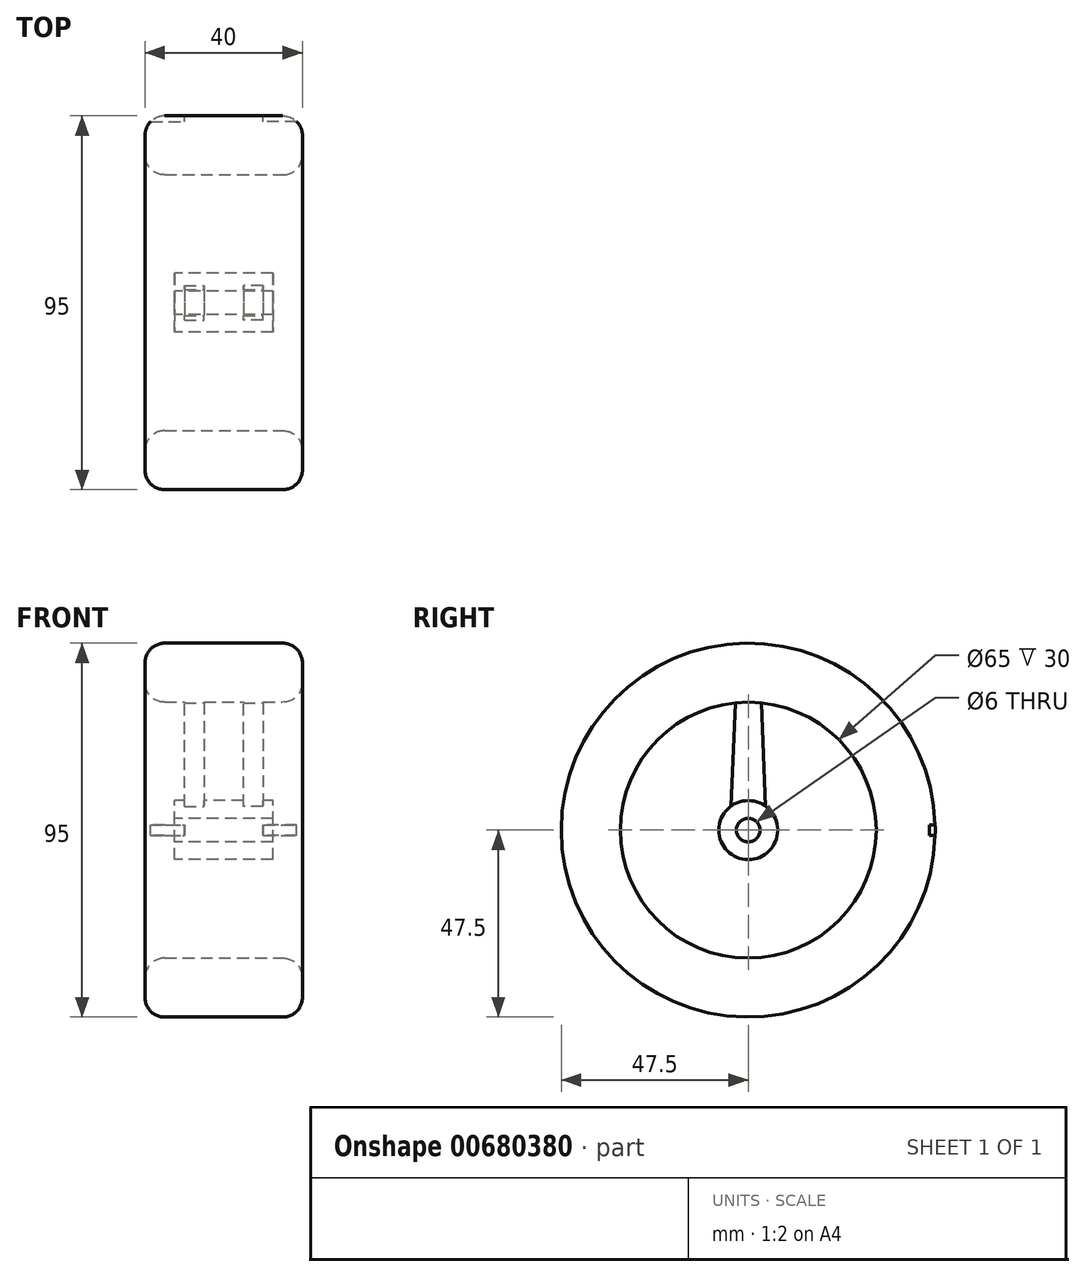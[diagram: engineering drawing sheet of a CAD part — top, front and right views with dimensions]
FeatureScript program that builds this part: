
annotation { "Feature Type Name" : "Feature", "Feature Type Description" : "" }
export const myFeature = defineFeature(function(context is Context, id is Id, definition is map)
    precondition{}
    {
        {
            var Q0;
            Q0=qCreatedBy(makeId("Right.planeOp"),FACE);
            var sketch = newSketch(context, id + "F0", { "sketchPlane" : qUnion([Q0])});
            skCircle(sketch, "E0", {"center": v(0, 0) * mm, "radius": 40 * mm});
            skPoint(sketch, "E1", {"position": v(0, 40) * mm});
            skPoint(sketch, "E2", {"position": v(0, -40) * mm});
            skSolve(sketch);
        }
        {
            var Q0;
            Q0=qCreatedBy(makeId("Front.planeOp"),FACE);
            var sketch = newSketch(context, id + "F1", { "sketchPlane" : qUnion([Q0])});
            skLineSegment(sketch, "E3.bottom", {"start": v(-15, 47.5) * mm, "end": v(15, 47.5) * mm});
            skLineSegment(sketch, "E3.top", {"start": v(-15, 32.5) * mm, "end": v(15, 32.5) * mm});
            skLineSegment(sketch, "E3.left", {"start": v(-20, 42.5) * mm, "end": v(-20, 37.5) * mm});
            skLineSegment(sketch, "E3.right", {"start": v(20, 42.5) * mm, "end": v(20, 37.5) * mm});
            skPoint(sketch, "E3.middle", {"position": v(0, 40) * mm});
            skPoint(sketch, "E4.visualSharp", {"position": v(-20, 47.5) * mm});
            skArc(sketch, "E4.filletArc", {"start": v(-15, 47.5) * mm, "mid": v(-18.54, 46.04) * mm, "end": v(-20, 42.5) * mm});
            skPoint(sketch, "E5.visualSharp", {"position": v(20, 32.5) * mm});
            skArc(sketch, "E5.filletArc", {"start": v(15, 32.5) * mm, "mid": v(18.54, 33.96) * mm, "end": v(20, 37.5) * mm});
            skPoint(sketch, "E6.visualSharp", {"position": v(-20, 32.5) * mm});
            skArc(sketch, "E6.filletArc", {"start": v(-20, 37.5) * mm, "mid": v(-18.54, 33.96) * mm, "end": v(-15, 32.5) * mm});
            skPoint(sketch, "E7.visualSharp", {"position": v(20, 47.5) * mm});
            skArc(sketch, "E7.filletArc", {"start": v(20, 42.5) * mm, "mid": v(18.54, 46.04) * mm, "end": v(15, 47.5) * mm});
            skLineSegment(sketch, "E8", {"start": v(44.27, 0) * mm, "end": v(-53.42, 0) * mm, "construction": true});
            skSolve(sketch);
        }
        {
            var Q0;
            Q0=qSketchRegion(id+"F1",true);
            var Q1;
            Q1=sQuery(id+"F0.wireOp",EDGE,"E0");
            sweep(context, id + "F2", {"profiles" : qUnion([Q0]), "path" : qUnion([Q1])});
        }
        {
            var Q0;
            Q0=qCreatedBy(makeId("Right.planeOp"),FACE);
            var sketch = newSketch(context, id + "F3", { "sketchPlane" : qUnion([Q0])});
            skLineSegment(sketch, "E9.bottom", {"start": v(46, 1.35) * mm, "end": v(49, 1.35) * mm});
            skLineSegment(sketch, "E9.top", {"start": v(46, -1.35) * mm, "end": v(49, -1.35) * mm});
            skLineSegment(sketch, "E9.left", {"start": v(46, 1.35) * mm, "end": v(46, -1.35) * mm});
            skLineSegment(sketch, "E9.right", {"start": v(49, 1.35) * mm, "end": v(49, -1.35) * mm});
            skPoint(sketch, "E9.middle", {"position": v(47.5, 0) * mm});
            skSolve(sketch);
        }
        {
            var Q0;
            Q0=makeQuery(id+"F3.imprint","IMPRINT",FACE,{"disambiguationData":[TD([[makeQuery(id+"F3.imprint","IMPRINT",EDGE,{"derivedFrom":sQuery(id+"F3.wireOp",EDGE,"E9.bottom")}),-1.0]])]});
            extrude(context, id + "F4", {"entities" : qUnion([Q0]), "operationType" : NewBodyOperationType.REMOVE, "oppositeDirection" : true, "depth" : 20 * mm, "offsetDistance" : 25 * mm, "hasSecondDirection" : true, "secondDirectionOppositeDirection" : true, "secondDirectionDepth" : 10 * mm});
        }
        {
            var Q0;
            Q0=makeQuery(id+"F3.imprint","IMPRINT",FACE,{"disambiguationData":[TD([[makeQuery(id+"F3.imprint","IMPRINT",EDGE,{"derivedFrom":sQuery(id+"F3.wireOp",EDGE,"E9.bottom")}),-1.0]])]});
            extrude(context, id + "F5", {"entities" : qUnion([Q0]), "operationType" : NewBodyOperationType.REMOVE, "depth" : 20 * mm, "offsetDistance" : 25 * mm, "hasSecondDirection" : true, "secondDirectionOppositeDirection" : true, "secondDirectionDepth" : -10 * mm});
        }
        {
            var Q0;
            Q0=qCreatedBy(makeId("Right.planeOp"),FACE);
            var sketch = newSketch(context, id + "F6", { "sketchPlane" : qUnion([Q0])});
            skCircle(sketch, "E10", {"center": v(0, 0) * mm, "radius": 7.5 * mm});
            skLineSegment(sketch, "E11", {"start": v(0, 0) * mm, "end": v(0, 37.37) * mm, "construction": true});
            skLineSegment(sketch, "E12", {"start": v(0, 0) * mm, "end": v(30.9, 10.04) * mm, "construction": true});
            skLineSegment(sketch, "E13", {"start": v(0, 0) * mm, "end": v(19.1, -26.3) * mm, "construction": true});
            skLineSegment(sketch, "E14", {"start": v(0, 0) * mm, "end": v(-19.1, -26.3) * mm, "construction": true});
            skLineSegment(sketch, "E15", {"start": v(0, 0) * mm, "end": v(-30.9, 10.04) * mm, "construction": true});
            skLineSegment(sketch, "E16", {"start": v(0, 0) * mm, "end": v(-19.1, 26.3) * mm, "construction": true});
            skLineSegment(sketch, "E17", {"start": v(0, 0) * mm, "end": v(19.1, 26.3) * mm, "construction": true});
            skLineSegment(sketch, "E18", {"start": v(-4.4, 6.07) * mm, "end": v(-3.1, 37.37) * mm});
            skLineSegment(sketch, "E19", {"start": v(-3.1, 37.37) * mm, "end": v(3.1, 37.37) * mm});
            skLineSegment(sketch, "E20", {"start": v(3.1, 37.37) * mm, "end": v(4.4, 6.07) * mm});
            skCircle(sketch, "E21", {"center": v(0, 0) * mm, "radius": 3 * mm});
            skSolve(sketch);
        }
        {
            var Q0;
            {var subQ0=sQuery(id+"F6.wireOp",EDGE,"E18");Q0=makeQuery(id+"F6.imprint","IMPRINT",FACE,{"disambiguationData":[TD([[makeQuery(id+"F6.imprint","IMPRINT",EDGE,{"derivedFrom":subQ0}),-1.0]])]});}
            extrude(context, id + "F7", {"entities" : qUnion([Q0]), "operationType" : NewBodyOperationType.ADD, "depth" : 10 * mm, "offsetDistance" : 25 * mm, "hasSecondDirection" : true, "secondDirectionOppositeDirection" : false, "secondDirectionDepth" : 5 * mm});
        }
        {
            var Q0;
            {var subQ0=sQuery(id+"F6.wireOp",EDGE,"E18");Q0=makeQuery(id+"F6.imprint","IMPRINT",FACE,{"disambiguationData":[TD([[makeQuery(id+"F6.imprint","IMPRINT",EDGE,{"derivedFrom":subQ0}),-1.0]])]});}
            extrude(context, id + "F8", {"entities" : qUnion([Q0]), "operationType" : NewBodyOperationType.ADD, "oppositeDirection" : true, "depth" : 10 * mm, "offsetDistance" : 25 * mm, "hasSecondDirection" : true, "secondDirectionOppositeDirection" : true, "secondDirectionDepth" : 5 * mm});
        }
        {
            var Q0;
            Q0=makeQuery(id+"F6.imprint","IMPRINT",FACE,{"disambiguationData":[TD([[makeQuery(id+"F6.imprint","IMPRINT",EDGE,{"derivedFrom":sQuery(id+"F6.wireOp",EDGE,"E21")}),-1.0]])]});
            extrude(context, id + "F9", {"entities" : qUnion([Q0]), "operationType" : NewBodyOperationType.ADD, "depth" : 25 * mm, "offsetDistance" : 25 * mm, "symmetric" : true});
        }
    });
